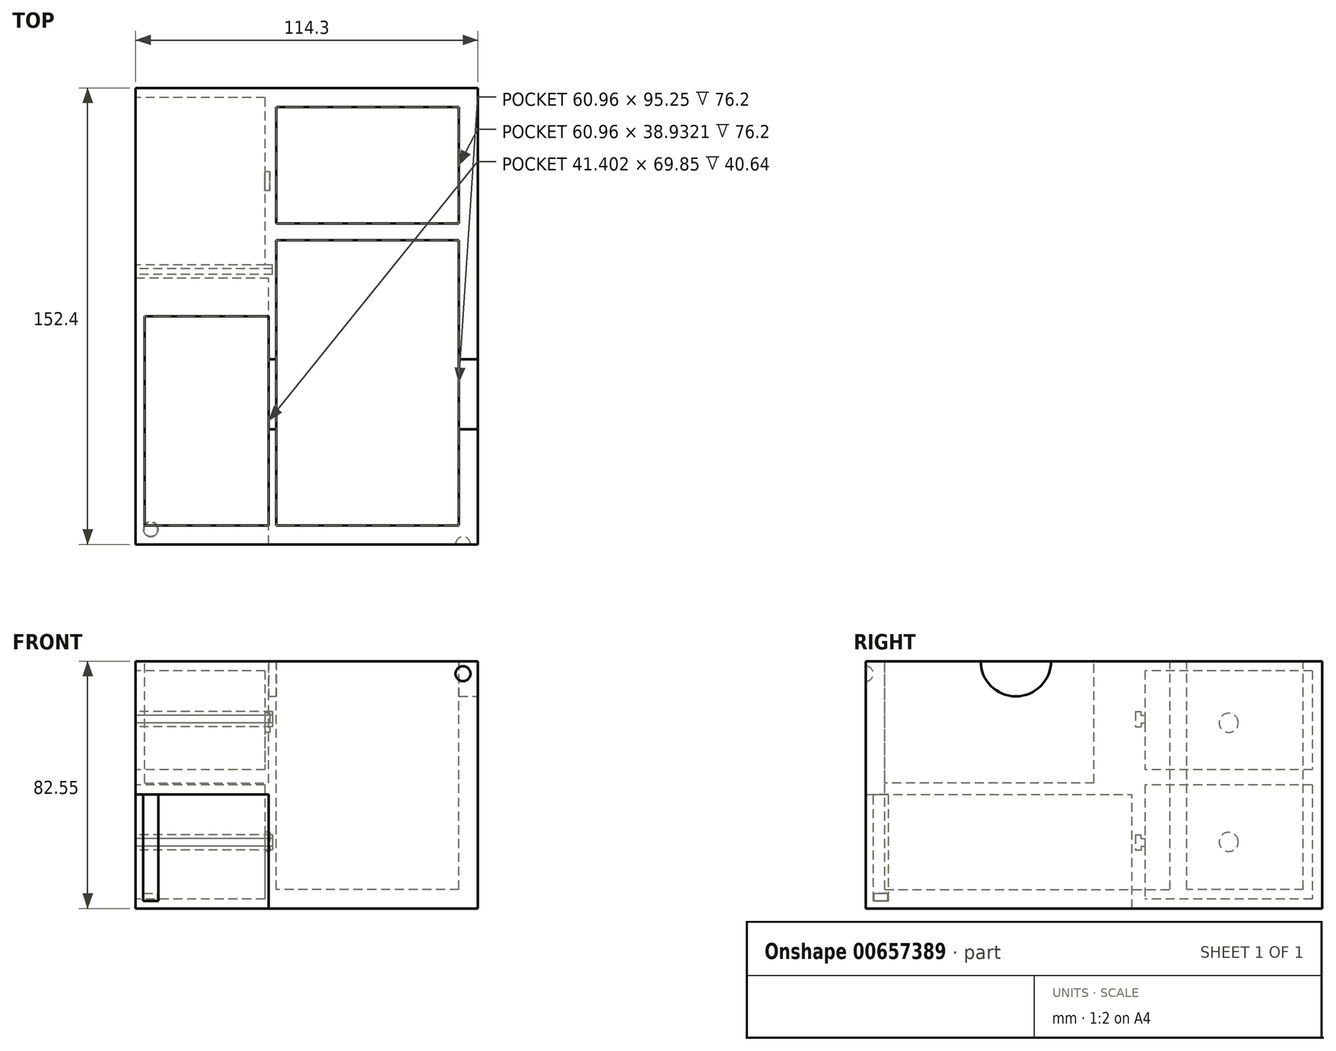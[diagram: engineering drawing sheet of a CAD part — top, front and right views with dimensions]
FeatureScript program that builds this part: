
annotation { "Feature Type Name" : "Feature", "Feature Type Description" : "" }
export const myFeature = defineFeature(function(context is Context, id is Id, definition is map)
    precondition{}
    {
        {
            var Q0;
            Q0=qCreatedBy(makeId("Top.planeOp"),FACE);
            var sketch = newSketch(context, id + "F0", { "sketchPlane" : qUnion([Q0])});
            skLineSegment(sketch, "E0.bottom", {"start": v(0, 0) * mm, "end": v(-114.3, 0) * mm});
            skLineSegment(sketch, "E0.top", {"start": v(0, 152.4) * mm, "end": v(-114.3, 152.4) * mm});
            skLineSegment(sketch, "E0.left", {"start": v(0, 0) * mm, "end": v(0, 152.4) * mm});
            skLineSegment(sketch, "E0.right", {"start": v(-114.3, 0) * mm, "end": v(-114.3, 152.4) * mm});
            skSolve(sketch);
        }
        {
            var Q0;
            Q0 = qSketchRegion(id + "F0", true);
            extrude(context, id + "F1", {"entities" : qUnion([Q0]), "oppositeDirection" : true, "depth" : 82.55 * mm, "offsetDistance" : 25.4 * mm});
        }
        {
            var Q0;
            Q0=makeQuery(id+"F1.opExtrude","CAP_FACE",FACE,{"disambiguationData":[OSD([sQuery(id+"F0.wireOp",EDGE,"E0.bottom"),sQuery(id+"F0.wireOp",EDGE,"E0.top"),sQuery(id+"F0.wireOp",EDGE,"E0.left"),sQuery(id+"F0.wireOp",EDGE,"E0.right")])],"isStart":true});
            var sketch = newSketch(context, id + "F2", { "sketchPlane" : qUnion([Q0])});
            skLineSegment(sketch, "E1.bottom", {"start": v(-6.35, 6.35) * mm, "end": v(-67.3, 6.35) * mm});
            skLineSegment(sketch, "E1.top", {"start": v(-6.35, 101.6) * mm, "end": v(-67.3, 101.6) * mm});
            skLineSegment(sketch, "E1.left", {"start": v(-6.35, 6.35) * mm, "end": v(-6.35, 101.6) * mm});
            skLineSegment(sketch, "E1.right", {"start": v(-67.3, 6.35) * mm, "end": v(-67.3, 101.6) * mm});
            skSolve(sketch);
        }
        {
            var Q0;
            Q0 = qSketchRegion(id + "F2", true);
            extrude(context, id + "F3", {"entities" : qUnion([Q0]), "operationType" : NewBodyOperationType.REMOVE, "oppositeDirection" : true, "depth" : 76.2 * mm, "offsetDistance" : 25.4 * mm});
        }
        {
            var Q0;
            Q0=makeQuery(id+"F1.opExtrude","SWEPT_FACE",FACE,{"disambiguationData":[OSD([sQuery(id+"F0.wireOp",EDGE,"E0.left")])]});
            var sketch = newSketch(context, id + "F4", { "sketchPlane" : qUnion([Q0])});
            skCircle(sketch, "E2", {"center": v(50.1, 0) * mm, "radius": 11.73 * mm});
            skSolve(sketch);
        }
        {
            var Q0;
            Q0 = qSketchRegion(id + "F4", true);
            extrude(context, id + "F5", {"entities" : qUnion([Q0]), "operationType" : NewBodyOperationType.REMOVE, "oppositeDirection" : true, "depth" : 75.18 * mm, "offsetDistance" : 25.4 * mm});
        }
        {
            var Q0;
            Q0=makeQuery(id+"F1.opExtrude","CAP_FACE",FACE,{"disambiguationData":[OSD([sQuery(id+"F0.wireOp",EDGE,"E0.bottom"),sQuery(id+"F0.wireOp",EDGE,"E0.top"),sQuery(id+"F0.wireOp",EDGE,"E0.left"),sQuery(id+"F0.wireOp",EDGE,"E0.right")])],"isStart":true});
            var sketch = newSketch(context, id + "F6", { "sketchPlane" : qUnion([Q0])});
            skPoint(sketch, "E3.oppositeSnap0", {"position": v(0, 107.12) * mm});
            skLineSegment(sketch, "E3.bottom", {"start": v(-67.3, 146.05) * mm, "end": v(-6.35, 146.05) * mm});
            skLineSegment(sketch, "E3.top", {"start": v(-67.3, 107.12) * mm, "end": v(-6.35, 107.12) * mm});
            skLineSegment(sketch, "E3.left", {"start": v(-67.3, 146.05) * mm, "end": v(-67.3, 107.12) * mm});
            skLineSegment(sketch, "E3.right", {"start": v(-6.35, 146.05) * mm, "end": v(-6.35, 107.12) * mm});
            skSolve(sketch);
        }
        {
            var Q0;
            Q0 = qSketchRegion(id + "F6", true);
            extrude(context, id + "F7", {"entities" : qUnion([Q0]), "operationType" : NewBodyOperationType.REMOVE, "oppositeDirection" : true, "depth" : 76.2 * mm, "offsetDistance" : 25.4 * mm});
        }
        {
            var Q0;
            Q0=makeQuery(id+"F1.opExtrude","SWEPT_FACE",FACE,{"disambiguationData":[OSD([sQuery(id+"F0.wireOp",EDGE,"E0.right")])]});
            var sketch = newSketch(context, id + "F8", { "sketchPlane" : qUnion([Q0])});
            skLineSegment(sketch, "E4.bottom", {"start": v(0, -82.55) * mm, "end": v(-88.9, -82.55) * mm});
            skLineSegment(sketch, "E4.top", {"start": v(0, -44.45) * mm, "end": v(-88.9, -44.45) * mm});
            skLineSegment(sketch, "E4.left", {"start": v(0, -82.55) * mm, "end": v(0, -44.45) * mm});
            skLineSegment(sketch, "E4.right", {"start": v(-88.9, -82.55) * mm, "end": v(-88.9, -44.45) * mm});
            skSolve(sketch);
        }
        {
            var Q0;
            Q0 = qSketchRegion(id + "F8", true);
            extrude(context, id + "F9", {"entities" : qUnion([Q0]), "operationType" : NewBodyOperationType.REMOVE, "oppositeDirection" : true, "depth" : 44.45 * mm, "offsetDistance" : 25.4 * mm});
        }
        {
            var Q0;
            Q0=makeQuery(id+"F1.opExtrude","SWEPT_FACE",FACE,{"disambiguationData":[OSD([sQuery(id+"F0.wireOp",EDGE,"E0.right")])]});
            var sketch = newSketch(context, id + "F10", { "sketchPlane" : qUnion([Q0])});
            skLineSegment(sketch, "E5.bottom", {"start": v(-149.13, -3.18) * mm, "end": v(-93.25, -3.17) * mm});
            skLineSegment(sketch, "E5.top", {"start": v(-149.13, -36.2) * mm, "end": v(-93.25, -36.2) * mm});
            skLineSegment(sketch, "E5.left", {"start": v(-149.13, -3.18) * mm, "end": v(-149.13, -36.2) * mm});
            skLineSegment(sketch, "E5.right", {"start": v(-93.25, -3.17) * mm, "end": v(-93.25, -36.2) * mm});
            skPoint(sketch, "E6.firstSnap0", {"position": v(-152.4, -41.28) * mm});
            skLineSegment(sketch, "E6.bottom", {"start": v(-149.13, -41.28) * mm, "end": v(-93.25, -41.28) * mm});
            skLineSegment(sketch, "E6.top", {"start": v(-149.13, -79.38) * mm, "end": v(-93.25, -79.38) * mm});
            skLineSegment(sketch, "E6.left", {"start": v(-149.13, -41.28) * mm, "end": v(-149.13, -79.38) * mm});
            skLineSegment(sketch, "E6.right", {"start": v(-93.25, -41.28) * mm, "end": v(-93.25, -79.38) * mm});
            skSolve(sketch);
        }
        {
            var Q0;
            Q0 = qSketchRegion(id + "F10", true);
            extrude(context, id + "F11", {"entities" : qUnion([Q0]), "operationType" : NewBodyOperationType.REMOVE, "oppositeDirection" : true, "depth" : 43.18 * mm, "offsetDistance" : 25.4 * mm});
        }
        {
            var Q0;
            Q0=makeQuery(id+"F9.boolean.opBoolean","COPY",FACE,{"derivedFrom":makeQuery(id+"F9.opExtrude","SWEPT_FACE",FACE,{"disambiguationData":[OSD([sQuery(id+"F8.wireOp",EDGE,"E4.top")])]})});
            var sketch = newSketch(context, id + "F12", { "sketchPlane" : qUnion([Q0])});
            skCircle(sketch, "E7", {"center": v(-109.26, -5.04) * mm, "radius": 2.5 * mm});
            skSolve(sketch);
        }
        {
            var Q0;
            Q0 = qSketchRegion(id + "F12", true);
            extrude(context, id + "F13", {"entities" : qUnion([Q0]), "operationType" : NewBodyOperationType.ADD, "depth" : 33.02 * mm, "offsetDistance" : 25.4 * mm});
        }
        {
            var Q0;
            Q0=makeQuery(id+"F13.opExtrude","CAP_FACE",FACE,{"disambiguationData":[OSD([sQuery(id+"F12.wireOp",EDGE,"E7")])],"isStart":false});
            var sketch = newSketch(context, id + "F14", { "sketchPlane" : qUnion([Q0])});
            skCircle(sketch, "E8", {"center": v(-109.26, -5.04) * mm, "radius": 2.5 * mm});
            skCircle(sketch, "E9", {"center": v(-109.26, -5.04) * mm, "radius": 2.3 * mm});
            skSolve(sketch);
        }
        {
            var Q0;
            Q0 = qSketchRegion(id + "F14", true);
            extrude(context, id + "F15", {"entities" : qUnion([Q0]), "operationType" : NewBodyOperationType.ADD, "depth" : 2.54 * mm, "offsetDistance" : 25.4 * mm});
        }
        {
            var Q0;
            Q0=makeQuery(id+"F1.opExtrude","SWEPT_FACE",FACE,{"disambiguationData":[OSD([sQuery(id+"F0.wireOp",EDGE,"E0.right")])]});
            var sketch = newSketch(context, id + "F16", { "sketchPlane" : qUnion([Q0])});
            skLineSegment(sketch, "E10.bottom", {"start": v(-91.98, -18.1) * mm, "end": v(-93.89, -18.1) * mm});
            skLineSegment(sketch, "E10.top", {"start": v(-91.98, -20.64) * mm, "end": v(-93.89, -20.64) * mm});
            skPoint(sketch, "E10.middle", {"position": v(-93.25, -19.69) * mm});
            skLineSegment(sketch, "E11.bottom", {"start": v(-90.08, -16.83) * mm, "end": v(-91.98, -16.83) * mm});
            skLineSegment(sketch, "E11.top", {"start": v(-90.08, -21.91) * mm, "end": v(-91.98, -21.91) * mm});
            skLineSegment(sketch, "E11.left", {"start": v(-90.08, -16.83) * mm, "end": v(-90.08, -21.91) * mm});
            skLineSegment(sketch, "E12", {"start": v(-91.98, -18.1) * mm, "end": v(-91.98, -16.83) * mm});
            skLineSegment(sketch, "E13", {"start": v(-91.98, -20.64) * mm, "end": v(-91.98, -21.91) * mm});
            skSolve(sketch);
        }
        {
            var Q0;
            Q0=makeQuery(id+"F16.imprint","IMPRINT",FACE,{"disambiguationData":[TD([[makeQuery(id+"F16.imprint","IMPRINT",EDGE,{"derivedFrom":sQuery(id+"F16.wireOp",EDGE,"E11.bottom")}),1.0]])]});
            extrude(context, id + "F17", {"entities" : qUnion([Q0]), "operationType" : NewBodyOperationType.REMOVE, "oppositeDirection" : true, "depth" : 45.72 * mm, "offsetDistance" : 25.4 * mm});
        }
        {
            var Q0;
            Q0=makeQuery(id+"F1.opExtrude","SWEPT_FACE",FACE,{"disambiguationData":[OSD([sQuery(id+"F0.wireOp",EDGE,"E0.right")])]});
            var sketch = newSketch(context, id + "F18", { "sketchPlane" : qUnion([Q0])});
            skLineSegment(sketch, "E14.bottom", {"start": v(-91.97, -59.23) * mm, "end": v(-93.88, -59.23) * mm});
            skLineSegment(sketch, "E14.top", {"start": v(-91.97, -61.77) * mm, "end": v(-93.88, -61.77) * mm});
            skPoint(sketch, "E14.middle", {"position": v(-93.24, -60.5) * mm});
            skLineSegment(sketch, "E15.bottom", {"start": v(-90.07, -57.96) * mm, "end": v(-91.97, -57.96) * mm});
            skLineSegment(sketch, "E15.top", {"start": v(-90.07, -63.04) * mm, "end": v(-91.97, -63.04) * mm});
            skLineSegment(sketch, "E15.left", {"start": v(-90.07, -57.96) * mm, "end": v(-90.07, -63.04) * mm});
            skLineSegment(sketch, "E16", {"start": v(-91.97, -59.23) * mm, "end": v(-91.97, -57.96) * mm});
            skLineSegment(sketch, "E17", {"start": v(-91.97, -61.77) * mm, "end": v(-91.97, -63.04) * mm});
            skSolve(sketch);
        }
        {
            var Q0;
            Q0 = qSketchRegion(id + "F18", true);
            var Q1;
            Q1=makeQuery(id+"F18.imprint","IMPRINT",FACE,{"disambiguationData":[TD([[makeQuery(id+"F18.imprint","IMPRINT",EDGE,{"derivedFrom":sQuery(id+"F18.wireOp",EDGE,"E15.bottom")}),1.0]])]});
            extrude(context, id + "F19", {"entities" : qUnion([Q0, Q1]), "operationType" : NewBodyOperationType.REMOVE, "oppositeDirection" : true, "depth" : 45.72 * mm, "offsetDistance" : 25.4 * mm});
        }
        {
            var Q0;
            Q0=makeQuery(id+"F11.boolean.opBoolean","COPY",FACE,{"derivedFrom":makeQuery(id+"F11.opExtrude","CAP_FACE",FACE,{"disambiguationData":[OSD([sQuery(id+"F10.wireOp",EDGE,"E5.bottom"),sQuery(id+"F10.wireOp",EDGE,"E5.top"),sQuery(id+"F10.wireOp",EDGE,"E5.left"),sQuery(id+"F10.wireOp",EDGE,"E5.right")])],"isStart":false})});
            var sketch = newSketch(context, id + "F20", { "sketchPlane" : qUnion([Q0])});
            skCircle(sketch, "E18", {"center": v(-121.2, -20.57) * mm, "radius": 3.2 * mm});
            skCircle(sketch, "E19", {"center": v(-121.2, -60.33) * mm, "radius": 3.2 * mm});
            skSolve(sketch);
        }
        {
            var Q0;
            Q0 = qSketchRegion(id + "F20", true);
            extrude(context, id + "F21", {"entities" : qUnion([Q0]), "operationType" : NewBodyOperationType.REMOVE, "oppositeDirection" : true, "depth" : 1.59 * mm, "offsetDistance" : 25.4 * mm});
        }
        {
            var Q0;
            Q0=makeQuery(id+"F1.opExtrude","CAP_FACE",FACE,{"disambiguationData":[OSD([sQuery(id+"F0.wireOp",EDGE,"E0.bottom"),sQuery(id+"F0.wireOp",EDGE,"E0.top"),sQuery(id+"F0.wireOp",EDGE,"E0.left"),sQuery(id+"F0.wireOp",EDGE,"E0.right")])],"isStart":true});
            var sketch = newSketch(context, id + "F22", { "sketchPlane" : qUnion([Q0])});
            skPoint(sketch, "E20.firstSnap0", {"position": v(-114.3, 76.2) * mm});
            skLineSegment(sketch, "E20.bottom", {"start": v(-111.3, 76.2) * mm, "end": v(-69.9, 76.2) * mm});
            skLineSegment(sketch, "E20.top", {"start": v(-111.3, 6.35) * mm, "end": v(-69.9, 6.35) * mm});
            skLineSegment(sketch, "E20.left", {"start": v(-111.3, 76.2) * mm, "end": v(-111.3, 6.35) * mm});
            skLineSegment(sketch, "E20.right", {"start": v(-69.9, 76.2) * mm, "end": v(-69.9, 6.35) * mm});
            skSolve(sketch);
        }
        {
            var Q0;
            Q0 = qSketchRegion(id + "F22", true);
            extrude(context, id + "F23", {"entities" : qUnion([Q0]), "operationType" : NewBodyOperationType.REMOVE, "oppositeDirection" : true, "depth" : 40.64 * mm, "offsetDistance" : 25.4 * mm});
        }
        {
            var Q0;
            Q0=makeQuery(id+"F1.opExtrude","SWEPT_FACE",FACE,{"disambiguationData":[OSD([sQuery(id+"F0.wireOp",EDGE,"E0.bottom")])]});
            var sketch = newSketch(context, id + "F24", { "sketchPlane" : qUnion([Q0])});
            skLineSegment(sketch, "E21", {"start": v(-114.3, 0) * mm, "end": v(0, -82.55) * mm, "construction": true});
            skLineSegment(sketch, "E22", {"start": v(0, 0) * mm, "end": v(-114.3, -82.55) * mm, "construction": true});
            skArc(sketch, "E23", {"start": v(-2.49, -4.19) * mm, "mid": v(-4.99, -1.69) * mm, "end": v(-7.49, -4.19) * mm});
            skLineSegment(sketch, "E24", {"start": v(-7.49, -4.19) * mm, "end": v(-2.49, -4.19) * mm, "construction": true});
            skLineSegment(sketch, "E25", {"start": v(-7.49, -4.19) * mm, "end": v(-2.49, -4.19) * mm});
            skSolve(sketch);
        }
        {
            var Q0;
            Q0 = qSketchRegion(id + "F24", true);
            var Q1;
            Q1=sQuery(id+"F24.wireOp",EDGE,"E25");
            revolve(context, id + "F25", {"operationType" : NewBodyOperationType.REMOVE, "entities" : qUnion([Q0]), "axis" : qUnion([Q1]), "revolveType" : RevolveType.FULL, "oppositeDirection" : true});
        }
    });
